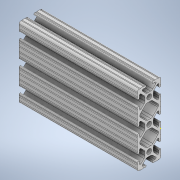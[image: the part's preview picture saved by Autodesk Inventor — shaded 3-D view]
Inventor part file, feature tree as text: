
AUTODESK INVENTOR PART (.ipt)
format: ipt  version: 2020 (Build 240168000, 168)  size: 369,152 bytes
history: native  units: in
note: dims shown in document units (in); Inventor stores cm internally (conversion verified against a paired STEP export)
features: sketch x2, extrude x1
ambient origin geometry x8: Origin, YZ Plane, XZ Plane, XY Plane, X Axis, Y Axis, Z Axis, Center Point
bodies: Solid1 (feature_tree)
feature tree (3):
  extrude  "Extrusion1"  [1 undecoded]
  sketch  "Sketch2"
  sketch  "Sketch1"  dims[d0=5.0in d1=0.0in]
note: 1 required parameter value undecoded (feature->parameter linkage not recoverable at this tier; creation-order binding heuristic only, values carry confidence <= 0.55)
